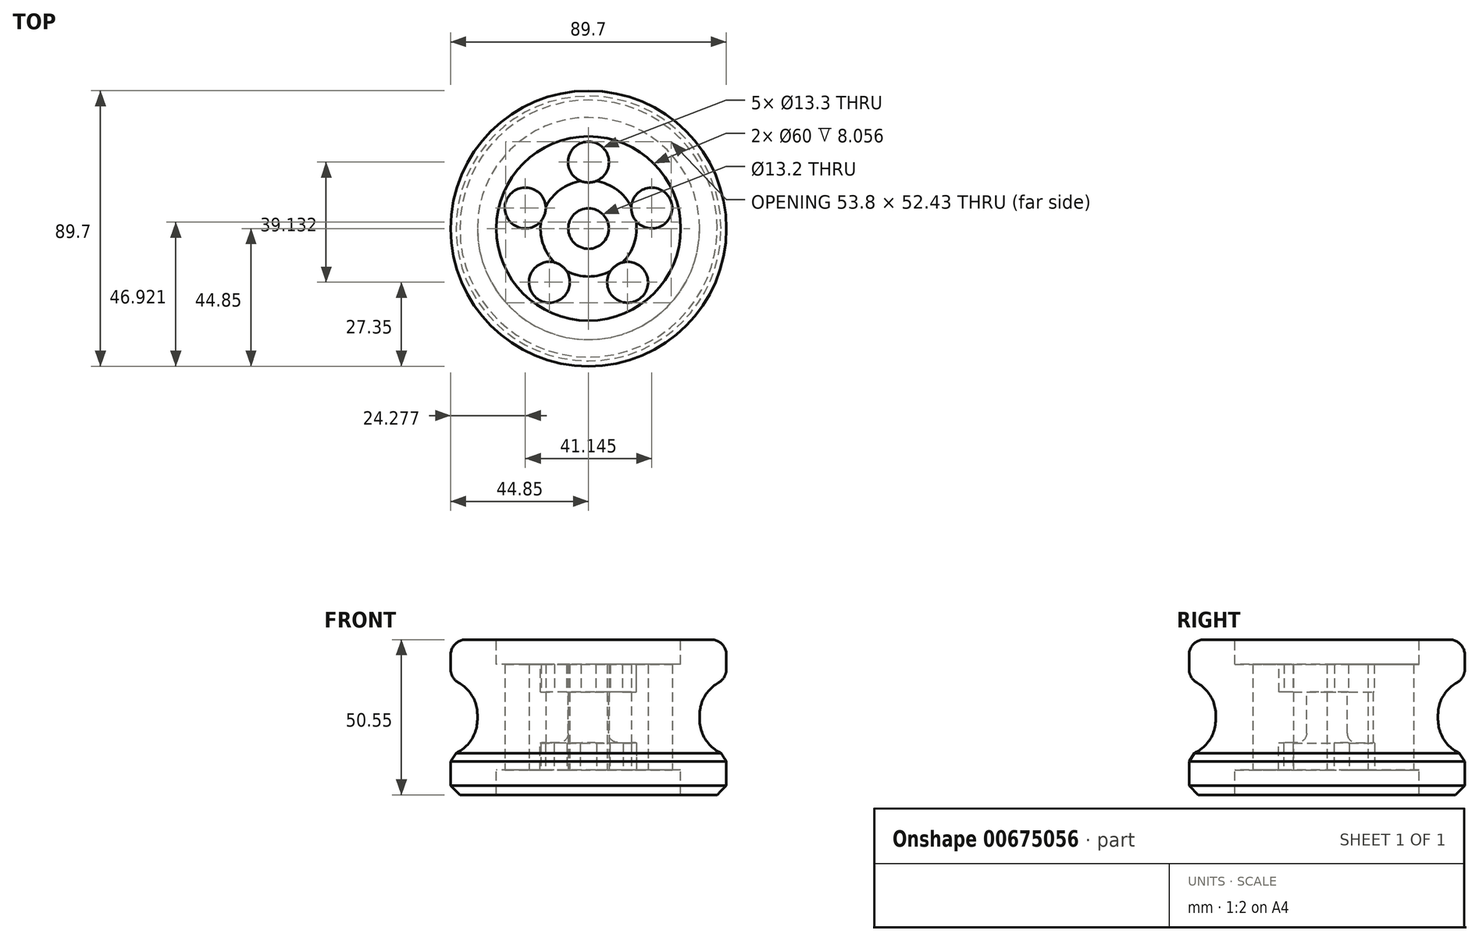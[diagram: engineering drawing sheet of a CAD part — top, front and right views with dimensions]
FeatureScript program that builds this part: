
annotation { "Feature Type Name" : "Feature", "Feature Type Description" : "" }
export const myFeature = defineFeature(function(context is Context, id is Id, definition is map)
    precondition{}
    {
        {
            var Q0;
            Q0=qCreatedBy(makeId("Front.planeOp"),FACE);
            var sketch = newSketch(context, id + "F0", { "sketchPlane" : qUnion([Q0])});
            skLineSegment(sketch, "E0", {"start": v(25.7, 25.27) * mm, "end": v(-60.8, 25.27) * mm, "construction": true});
            skLineSegment(sketch, "E1", {"start": v(-6.6, 33.43) * mm, "end": v(-15.63, 33.43) * mm});
            skLineSegment(sketch, "E2", {"start": v(-15.63, 33.43) * mm, "end": v(-15.63, 42.5) * mm});
            skLineSegment(sketch, "E3", {"start": v(-15.63, 42.5) * mm, "end": v(-30, 42.5) * mm});
            skLineSegment(sketch, "E4", {"start": v(-30, 42.5) * mm, "end": v(-30, 50.55) * mm});
            skLineSegment(sketch, "E5", {"start": v(-30, 50.55) * mm, "end": v(-44.85, 50.55) * mm});
            skLineSegment(sketch, "E6", {"start": v(-44.85, 50.55) * mm, "end": v(-44.85, 37.6) * mm});
            skLineSegment(sketch, "E7", {"start": v(-36.16, 37.6) * mm, "end": v(-36.16, 25.27) * mm});
            skLineSegment(sketch, "E8.MirrorCS", {"start": v(-30, 8.06) * mm, "end": v(-30, 0) * mm});
            skLineSegment(sketch, "E9.MirrorCS", {"start": v(-44.85, 12.95) * mm, "end": v(-36.16, 12.95) * mm});
            skLineSegment(sketch, "E10.MirrorCS", {"start": v(-15.75, 8.06) * mm, "end": v(-30, 8.06) * mm});
            skLineSegment(sketch, "E11.MirrorCS", {"start": v(-36.16, 12.95) * mm, "end": v(-36.16, 25.27) * mm});
            skLineSegment(sketch, "E12.MirrorCS", {"start": v(-44.85, 0) * mm, "end": v(-44.85, 12.95) * mm});
            skLineSegment(sketch, "E13.MirrorCS", {"start": v(-15.75, 16.9) * mm, "end": v(-15.75, 8.06) * mm});
            skLineSegment(sketch, "E14.MirrorCS", {"start": v(-30, 0) * mm, "end": v(-44.85, 0) * mm});
            skLineSegment(sketch, "E15.MirrorCS", {"start": v(-6.6, 17.08) * mm, "end": v(-15.75, 16.9) * mm});
            skLineSegment(sketch, "E16.MirrorCS", {"start": v(-6.6, 25.27) * mm, "end": v(-6.6, 17.08) * mm});
            skLineSegment(sketch, "E17", {"start": v(0, 45.37) * mm, "end": v(0, -31.44) * mm, "construction": true});
            skLineSegment(sketch, "E18", {"start": v(-30, 0) * mm, "end": v(0, 0) * mm, "construction": true});
            skLineSegment(sketch, "E19", {"start": v(-44.85, 37.6) * mm, "end": v(-36.16, 37.6) * mm});
            skLineSegment(sketch, "E20", {"start": v(-6.6, 25.27) * mm, "end": v(-6.6, 33.43) * mm});
            skLineSegment(sketch, "E21", {"start": v(-36.16, 25.27) * mm, "end": v(-9.94, 25.27) * mm});
            skSolve(sketch);
        }
        {
            var Q0;
            Q0=makeQuery(id+"F0.imprint","IMPRINT",FACE,{"disambiguationData":[TD([[makeQuery(id+"F0.imprint","IMPRINT",EDGE,{"derivedFrom":sQuery(id+"F0.wireOp",EDGE,"E1")}),1.0]])]});
            var Q1;
            Q1=sQuery(id+"F0.wireOp",EDGE,"E17");
            revolve(context, id + "F1", {"entities" : qUnion([Q0]), "axis" : qUnion([Q1]), "revolveType" : RevolveType.FULL});
        }
        {
            var Q0;
            Q0=makeQuery(id+"F1.opRevolve","SWEPT_FACE",FACE,{"disambiguationData":[OSD([sQuery(id+"F0.wireOp",EDGE,"E7"),sQuery(id+"F0.wireOp",EDGE,"E11.MirrorCS")])]});
            fillet(context, id + "F2", {"entities" : qUnion([Q0]), "radius" : 12 * mm, "tangentPropagation" : true, "allowEdgeOverflow" : false});
        }
        {
            var Q0;
            Q0=qCreatedBy(makeId("Top.planeOp"),FACE);
            var sketch = newSketch(context, id + "F3", { "sketchPlane" : qUnion([Q0])});
            skCircle(sketch, "E22", {"center": v(0, 0) * mm, "radius": 14.61 * mm, "construction": true});
            skCircle(sketch, "E23", {"center": v(0, 0) * mm, "radius": 28.65 * mm, "construction": true});
            skLineSegment(sketch, "E24", {"start": v(0, 0) * mm, "end": v(0, 3.72) * mm, "construction": true});
            skLineSegment(sketch, "E25.trimOffspring", {"start": v(0, 14.61) * mm, "end": v(0, 28.65) * mm, "construction": true});
            skCircle(sketch, "E26", {"center": v(0, 21.63) * mm, "radius": 6.65 * mm});
            skCircle(sketch, "E27.1.0", {"center": v(-20.57, 6.68) * mm, "radius": 6.65 * mm});
            skCircle(sketch, "E27.2.0", {"center": v(-12.71, -17.5) * mm, "radius": 6.65 * mm});
            skCircle(sketch, "E27.3.0", {"center": v(12.71, -17.5) * mm, "radius": 6.65 * mm});
            skCircle(sketch, "E27.4.0", {"center": v(20.57, 6.68) * mm, "radius": 6.65 * mm});
            skSolve(sketch);
        }
        {
            var Q0;
            Q0=makeQuery(id+"F3.imprint","IMPRINT",FACE,{"disambiguationData":[TD([[makeQuery(id+"F3.imprint","IMPRINT",EDGE,{"derivedFrom":sQuery(id+"F3.wireOp",EDGE,"E27.2.0")}),1.0]])]});
            var Q1;
            Q1=makeQuery(id+"F3.imprint","IMPRINT",FACE,{"disambiguationData":[TD([[makeQuery(id+"F3.imprint","IMPRINT",EDGE,{"derivedFrom":sQuery(id+"F3.wireOp",EDGE,"E27.3.0")}),1.0]])]});
            var Q2;
            Q2=makeQuery(id+"F3.imprint","IMPRINT",FACE,{"disambiguationData":[TD([[makeQuery(id+"F3.imprint","IMPRINT",EDGE,{"derivedFrom":sQuery(id+"F3.wireOp",EDGE,"E27.4.0")}),1.0]])]});
            var Q3;
            Q3=makeQuery(id+"F3.imprint","IMPRINT",FACE,{"disambiguationData":[TD([[makeQuery(id+"F3.imprint","IMPRINT",EDGE,{"derivedFrom":sQuery(id+"F3.wireOp",EDGE,"E26")}),1.0]])]});
            var Q4;
            Q4=makeQuery(id+"F3.imprint","IMPRINT",FACE,{"disambiguationData":[TD([[makeQuery(id+"F3.imprint","IMPRINT",EDGE,{"derivedFrom":sQuery(id+"F3.wireOp",EDGE,"E27.1.0")}),1.0]])]});
            extrude(context, id + "F4", {"entities" : qUnion([Q0, Q1, Q2, Q3, Q4]), "operationType" : NewBodyOperationType.REMOVE, "depth" : 50 * mm, "offsetDistance" : 25 * mm});
        }
        {
            var Q0;
            Q0=makeQuery(id+"F1.opRevolve","SWEPT_EDGE",EDGE,{"disambiguationData":[OSD([sQuery(id+"F0.wireOp",EDGE,"E15.MirrorCS"),sQuery(id+"F0.wireOp",EDGE,"E16.MirrorCS")])]});
            fillet(context, id + "F5", {"entities" : qUnion([Q0]), "radius" : 3 * mm, "tangentPropagation" : true, "allowEdgeOverflow" : false});
        }
        {
            var Q0;
            Q0=makeQuery(id+"F1.opRevolve","SWEPT_FACE",FACE,{"disambiguationData":[OSD([sQuery(id+"F0.wireOp",EDGE,"E6")])]});
            fillet(context, id + "F6", {"entities" : qUnion([Q0]), "radius" : 5 * mm, "tangentPropagation" : true, "allowEdgeOverflow" : false});
        }
        {
            var Q0;
            Q0=makeQuery(id+"F1.opRevolve","SWEPT_FACE",FACE,{"disambiguationData":[OSD([sQuery(id+"F0.wireOp",EDGE,"E12.MirrorCS")])]});
            chamfer(context, id + "F7", {"entities" : qUnion([Q0]), "width" : 3 * mm, "tangentPropagation" : true});
        }
    });
